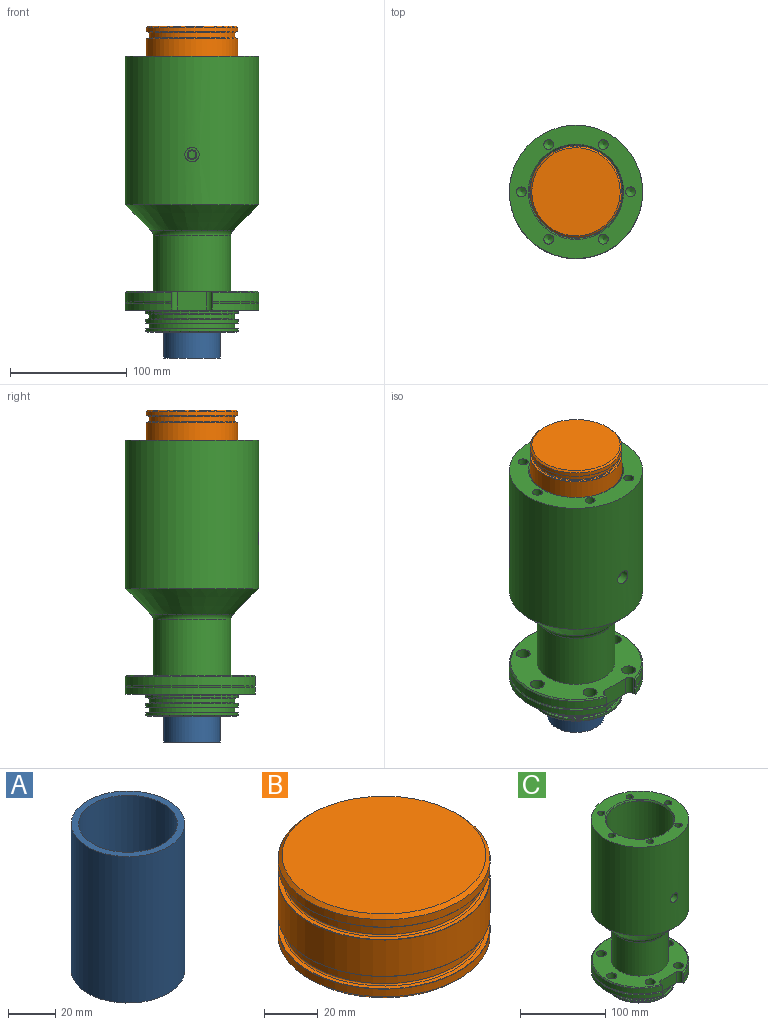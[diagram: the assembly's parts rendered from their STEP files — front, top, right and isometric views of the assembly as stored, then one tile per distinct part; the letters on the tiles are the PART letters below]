
ASSEMBLY  parts=3 mates=2
PART A: 9 faces, bbox 48.3x48.3x76.2 mm
  f0: plane 48.26x48.26mm, normal (0,0,-1), area 1702.5mm2, adj f4,f5,f6,f7,f8
  f1: plane 41.91x41.91mm, normal (0,0,1), area 1252.8mm2, adj f2,f5,f6,f7,f8
  f2: cylinder r=20.96mm len=69.85mm, axis (0,0,-1), area 9196.7mm2, adj f1,f3
  f3: plane 48.26x48.26mm, normal (0,0,1), area 449.7mm2, adj f2,f4
  f4: cylinder r=24.13mm len=76.2mm, axis (0,0,-1), area 11552.9mm2, adj f0,f3
  f5: cylinder r=3.17mm len=6.35mm, axis (0,0,-1), area 126.7mm2, adj f0,f1
  f6: cylinder r=3.17mm len=6.35mm, axis (0,0,-1), area 126.7mm2, adj f0,f1
  f7: cylinder r=3.17mm len=6.35mm, axis (0,0,-1), area 126.7mm2, adj f0,f1
  f8: cylinder r=3.17mm len=6.35mm, axis (0,0,-1), area 126.7mm2, adj f0,f1
PART B: 21 faces, bbox 85.2x85.2x38.1 mm
  f0: cylinder r=36.86mm len=73.71mm, axis (0,0,1), area 999.9mm2, adj f1,f20
  f1: torus R=37.49mm, axis (0,0,1), area 232.4mm2, adj f0,f2
  f2: plane 78.49x78.49mm, normal (0,0,1), area 422.5mm2, adj f1,f3
  f3: torus R=39.24mm, axis (0,0,1), area 49.3mm2, adj f2,f4
  f4: cylinder r=39.37mm len=78.74mm, axis (0,0,1), area 4084.1mm2, adj f3,f5
  f5: torus R=39.24mm, axis (0,0,1), area 49.3mm2, adj f4,f6
  f6: plane 78.49x78.49mm, normal (0,0,-1), area 422.5mm2, adj f5,f7
  f7: torus R=37.49mm, axis (0,0,1), area 232.4mm2, adj f6,f8
  f8: cylinder r=36.86mm len=73.71mm, axis (0,0,1), area 999.9mm2, adj f7,f9
  f9: torus R=37.49mm, axis (0,0,1), area 232.4mm2, adj f8,f10
  f10: plane 78.49x78.49mm, normal (0,0,1), area 422.5mm2, adj f9,f11
  f11: torus R=39.24mm, axis (0,0,1), area 49.3mm2, adj f10,f12
  f12: cylinder r=39.37mm len=78.74mm, axis (0,0,1), area 848.2mm2, adj f11,f13
  f13: cone r=39.37mm half-angle=45deg, axis (0,0,1), area 522.8mm2, adj f12,f14
  f14: plane 75.69x75.69mm, normal (0,0,-1), area 4499.8mm2, adj f13
  f15: plane 75.69x75.69mm, normal (0,0,1), area 4499.8mm2, adj f16
  f16: cone r=39.37mm half-angle=45deg, axis (0,0,-1), area 522.8mm2, adj f15,f17
  f17: cylinder r=39.37mm len=78.74mm, axis (0,0,1), area 848.2mm2, adj f16,f18
  f18: torus R=39.24mm, axis (0,0,1), area 49.3mm2, adj f17,f19
  f19: plane 78.49x78.49mm, normal (0,0,-1), area 422.5mm2, adj f18,f20
  f20: torus R=37.49mm, axis (0,0,1), area 232.4mm2, adj f0,f19
PART C: 73 faces, bbox 124.9x121.9x236.6 mm
  f0: cylinder r=3.45mm len=7.11mm, axis (0,-1,0), area 153.4mm2, adj f1,f67,f70,f71
  f1: cylinder r=39.74mm len=123.19mm, axis (0,0,-1), area 30720mm2, adj f0,f17,f18,f67,f70
  f2: cylinder r=57.15mm len=127mm, axis (0,0,-1), area 45484.2mm2, adj f20,f21,f69
  f3: cylinder r=57.15mm len=114.3mm, axis (0,0,-1), area 2527mm2, adj f6,f7,f62,f63
  f4: cylinder r=57.15mm len=114.3mm, axis (0,0,-1), area 1807.5mm2, adj f7,f8,f62,f63
  f5: plane 112.14x109.34mm, normal (0,0,1), area 5443mm2, adj f6,f23,f51,f52,f53,f54,f55,f56
  f6: cone r=57.15mm half-angle=45deg, axis (0,0,-1), area 487.8mm2, adj f3,f5,f62,f63
  f7: torus R=57.15mm, axis (0,0,-1), area 766.9mm2, adj f3,f4,f62,f63
  f8: plane 114.3x111.55mm, normal (0,0,-1), area 4347.6mm2, adj f4,f24,f51,f52,f53,f54,f55,f56
  f9: plane 79.1x79.1mm, normal (0,0,1), area 521.8mm2, adj f10,f38
  f10: torus R=39.55mm, axis (0,0,-1), area 49.7mm2, adj f9,f11
  f11: cylinder r=39.67mm len=79.35mm, axis (0,0,-1), area 459.5mm2, adj f10,f12
  f12: cone r=39.67mm half-angle=45deg, axis (0,0,1), area 374.7mm2, adj f11,f13
  f13: plane 77.19x77.19mm, normal (0,0,-1), area 1545.2mm2, adj f12,f14
  f14: cone r=31.59mm half-angle=30deg, axis (0,0,-1), area 2572.9mm2, adj f13,f15
  f15: cylinder r=24.26mm len=88.9mm, axis (0,0,-1), area 13549.4mm2, adj f14,f16
  f16: plane 48.51x48.51mm, normal (0,0,-1), area 1690.2mm2, adj f15,f57,f58,f59,f60,f61
  f17: plane 79.48x79.48mm, normal (0,0,1), area 4802.6mm2, adj f1,f57,f58,f59,f60,f61
  f18: torus R=39.99mm, axis (0,0,-1), area 33.2mm2, adj f1,f19
  f19: cone r=39.77mm half-angle=30deg, axis (0,0,1), area 539.8mm2, adj f18,f20
  f20: plane 114.3x114.3mm, normal (0,0,1), area 4686.3mm2, adj f2,f19,f40,f42,f44,f46,f48,f50
  f21: cone r=57.15mm half-angle=45deg, axis (0,0,1), area 8987mm2, adj f2,f22
  f22: torus R=39.75mm, axis (0,0,-1), area 1066.5mm2, adj f21,f23
  f23: cylinder r=33.4mm len=66.8mm, axis (0,0,-1), area 10109.1mm2, adj f5,f22
  f24: torus R=39.67mm, axis (0,0,-1), area 394.6mm2, adj f8,f25
  f25: cylinder r=39.67mm len=79.35mm, axis (0,0,-1), area 474.9mm2, adj f24,f26
  f26: torus R=39.55mm, axis (0,0,-1), area 49.7mm2, adj f25,f27
  f27: plane 79.1x79.1mm, normal (0,0,-1), area 521.8mm2, adj f26,f28
  f28: torus R=37.39mm, axis (0,0,-1), area 185.8mm2, adj f27,f29
  f29: cylinder r=36.88mm len=73.76mm, axis (0,0,-1), area 882.9mm2, adj f28,f30
  f30: torus R=37.39mm, axis (0,0,-1), area 185.8mm2, adj f29,f31
  f31: plane 79.1x79.1mm, normal (0,0,1), area 521.8mm2, adj f30,f32
  f32: torus R=39.55mm, axis (0,0,-1), area 49.7mm2, adj f31,f33
  f33: cylinder r=39.67mm len=79.35mm, axis (0,0,-1), area 759.8mm2, adj f32,f34
  f34: torus R=39.55mm, axis (0,0,-1), area 49.7mm2, adj f33,f35
  f35: plane 79.1x79.1mm, normal (0,0,-1), area 521.8mm2, adj f34,f36
  f36: torus R=37.39mm, axis (0,0,-1), area 185.8mm2, adj f35,f37
  f37: cylinder r=36.88mm len=73.76mm, axis (0,0,-1), area 882.9mm2, adj f36,f38
  f38: torus R=37.39mm, axis (0,0,-1), area 185.8mm2, adj f9,f37
  f39: cone r=0mm half-angle=59deg, axis (0,0,1), area 65.2mm2, adj f40
  f40: cylinder r=4.22mm len=34.93mm, axis (0,0,1), area 925.2mm2, adj f20,f39
  f41: cone r=0mm half-angle=59deg, axis (0,0,1), area 65.2mm2, adj f42
  f42: cylinder r=4.22mm len=34.93mm, axis (0,0,1), area 925.2mm2, adj f20,f41
  f43: cone r=0mm half-angle=59deg, axis (0,0,1), area 65.2mm2, adj f44
  f44: cylinder r=4.22mm len=34.93mm, axis (0,0,1), area 925.2mm2, adj f20,f43
  f45: cone r=0mm half-angle=59deg, axis (0,0,1), area 65.2mm2, adj f46
  f46: cylinder r=4.22mm len=34.93mm, axis (0,0,1), area 925.2mm2, adj f20,f45
  f47: cone r=0mm half-angle=59deg, axis (0,0,1), area 65.2mm2, adj f48
  f48: cylinder r=4.22mm len=34.93mm, axis (0,0,1), area 925.2mm2, adj f20,f47
  f49: cone r=0mm half-angle=59deg, axis (0,0,1), area 65.2mm2, adj f50
  f50: cylinder r=4.22mm len=34.93mm, axis (0,0,1), area 925.2mm2, adj f20,f49
  f51: cylinder r=5.97mm len=16mm, axis (0,0,1), area 600.1mm2, adj f5,f8
  f52: cylinder r=5.97mm len=16mm, axis (0,0,1), area 600.1mm2, adj f5,f8
  f53: cylinder r=5.97mm len=16mm, axis (0,0,1), area 600.1mm2, adj f5,f8
  f54: cylinder r=5.97mm len=16mm, axis (0,0,1), area 600.1mm2, adj f5,f8
  f55: cylinder r=5.97mm len=16mm, axis (0,0,1), area 600.1mm2, adj f5,f8
  f56: cylinder r=5.97mm len=16mm, axis (0,0,1), area 600.1mm2, adj f5,f8
  f57: cylinder r=3.17mm len=9.84mm, axis (0,0,1), area 196.3mm2, adj f16,f17
  f58: cylinder r=3.17mm len=9.84mm, axis (0,0,1), area 196.3mm2, adj f16,f17
  f59: cylinder r=3.17mm len=9.84mm, axis (0,0,1), area 196.3mm2, adj f16,f17
  f60: cylinder r=3.17mm len=9.84mm, axis (0,0,1), area 196.3mm2, adj f16,f17
  f61: cylinder r=3.17mm len=9.84mm, axis (0,0,1), area 196.3mm2, adj f16,f17
  f62: plane 16.01x2.08mm, normal (1,0,0), area 31.6mm2, adj f3,f4,f5,f6,f7,f8,f66
  f63: plane 16.01x2.08mm, normal (-1,0,0), area 31.6mm2, adj f3,f4,f5,f6,f7,f8,f64
  f64: cylinder r=4.83mm len=16mm, axis (0,0,1), area 121.3mm2, adj f5,f8,f63,f65
  f65: plane 25.4x16mm, normal (0,-1,0), area 406.5mm2, adj f5,f8,f64,f66
  f66: cylinder r=4.83mm len=16mm, axis (0,0,1), area 121.3mm2, adj f5,f8,f62,f65
  f67: cone r=0mm half-angle=59deg, axis (0,-1,0), area 0.1mm2, adj f0,f1
  f68: plane 12.29x12.29mm, normal (0,-1,0), area 64.2mm2, adj f69,f72
  f69: cylinder r=6.15mm len=12.29mm, axis (0,-1,0), area 307.5mm2, adj f2,f68
  f70: cone r=0mm half-angle=59deg, axis (0,-1,0), area 0.1mm2, adj f0,f1
  f71: plane 8.33x8.33mm, normal (0,-1,0), area 17mm2, adj f0,f72
  f72: cylinder r=4.17mm len=8.33mm, axis (0,-1,0), area 59.8mm2, adj f68,f71
PLACE A t=(0,0,-22)mm
PLACE B t=(0,0,224.65)mm
PLACE C at identity fixed
MATE slider B.f0 <-> C.f1  axis (0,0,1) through (0,0,243.7)mm
MATE slider A.f2 <-> C.f1  axis (0,0,-1) through (0,0,16.1)mm
